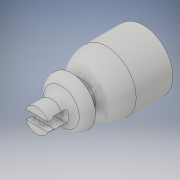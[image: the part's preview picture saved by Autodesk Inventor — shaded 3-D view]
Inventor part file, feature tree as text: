
AUTODESK INVENTOR PART (.ipt)
format: ipt  version: 2018 (Build 220112000, 112)  size: 193,024 bytes
history: native  units: mm
features: extrude x10, sketch x10, fillet x3
ambient origin geometry x8: Origin, YZ Plane, XZ Plane, XY Plane, X Axis, Y Axis, Z Axis, Center Point
bodies: Volumenkörper1 (feature_tree)
feature tree (23):
  extrude  "Extrusion1"  Depth=2.0mm TaperAngle=0.0deg
  fillet  "Rundung1"  Radius=2.0mm
  extrude  "Extrusion2"  Depth=1.5mm TaperAngle=0.0deg
  extrude  "Extrusion3"  Depth=10.0mm TaperAngle=0.0deg
  extrude  "Extrusion5"  Depth=10.0mm TaperAngle=0.0deg
  extrude  "Extrusion6"  Depth=2.5mm TaperAngle=0.0deg
  extrude  "Extrusion7"  Depth=1.6mm TaperAngle=0.0deg
  fillet  "Rundung2"  Radius=5.0mm
  extrude  "Extrusion8"  Depth=4.0mm TaperAngle=0.0deg
  extrude  "Extrusion9"  Depth=4.0mm
  extrude  "Extrusion10"  Depth=1.0mm TaperAngle=0.0deg
  extrude  "Extrusion11"  [1 undecoded]
  fillet  "Rundung3"  [1 undecoded]
  sketch  "Skizze1"  dims[d0=8.0mm d1=2.0mm d2=0.0mm d3=2.0mm]
  sketch  "Skizze2"  dims[d4=5.0mm d5=1.5mm d6=0.0mm]
  sketch  "Skizze3"  dims[d7=10.0mm d8=8.0mm d9=0.0mm]
  sketch  "Skizze5"  dims[d13=10.0mm d14=2.5mm d15=0.0mm]
  sketch  "Skizze6"  dims[d16=8.5mm d17=2.5mm d18=0.0mm]
  sketch  "Skizze8"  dims[d19=1.6mm d20=1.6mm d21=0.0mm d22=5.0mm]
  sketch  "Skizze11"  dims[d23=4.0mm d24=2.85mm d25=0.0mm]
  sketch  "Skizze12"  dims[d26=2.15mm d27=0.0mm d28=4.0mm]
  sketch  "Skizze13"  dims[d29=1.0mm d30=0.0mm d31=1.0mm d32=0.0mm]
  sketch  "Skizze14"  dims[d33=2.0mm]
note: 2 required parameter values undecoded (feature->parameter linkage not recoverable at this tier; creation-order binding heuristic only, values carry confidence <= 0.55)
